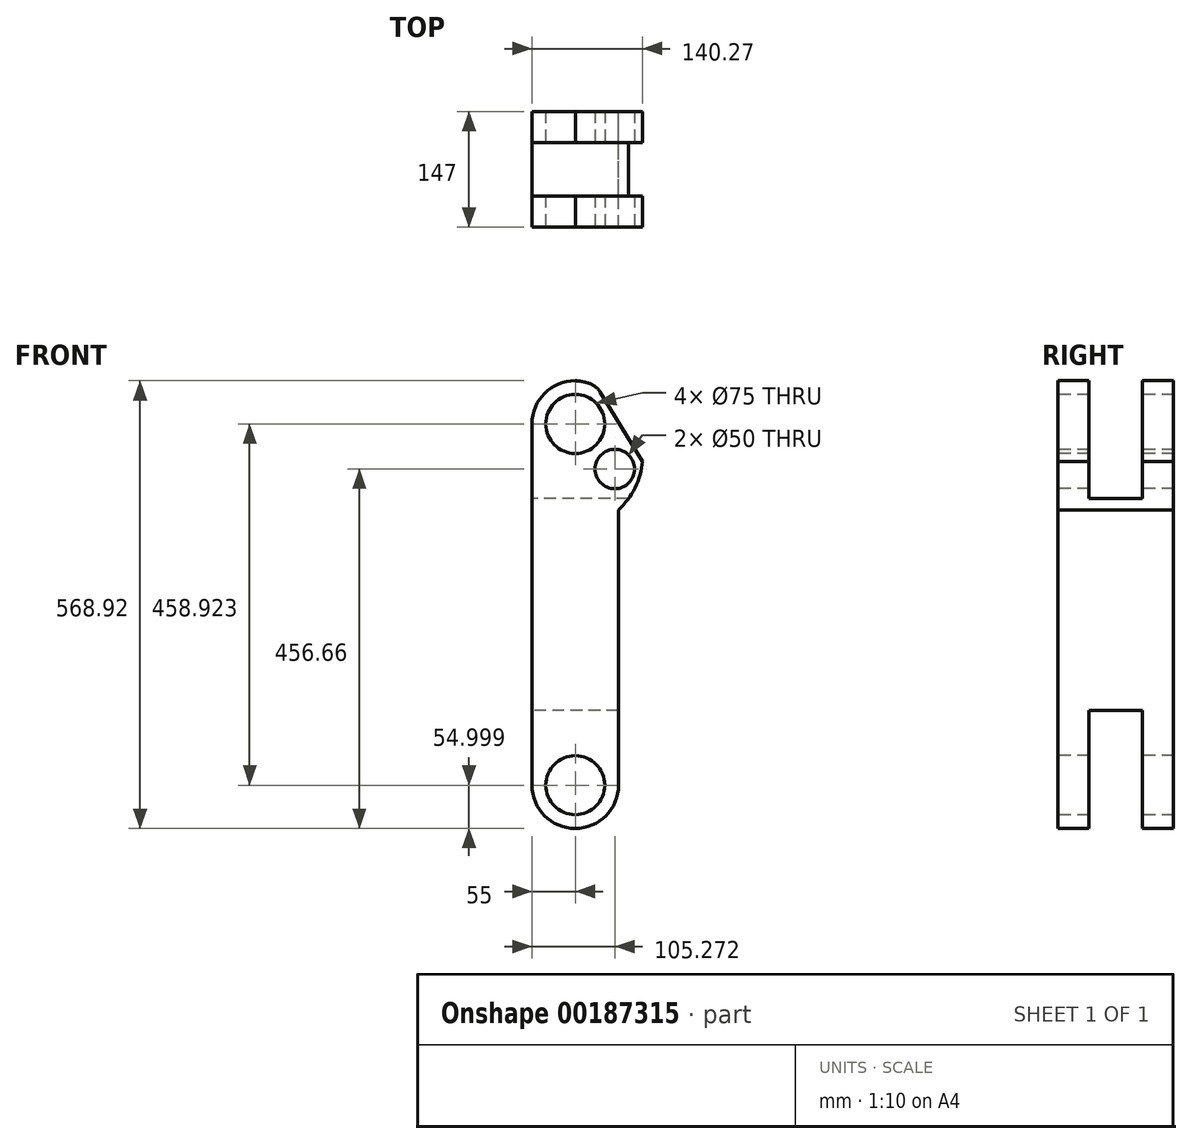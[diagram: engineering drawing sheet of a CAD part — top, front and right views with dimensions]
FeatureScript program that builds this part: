
annotation { "Feature Type Name" : "Feature", "Feature Type Description" : "" }
export const myFeature = defineFeature(function(context is Context, id is Id, definition is map)
    precondition{}
    {
        {
            var Q0;
            Q0=qCreatedBy(makeId("Front.planeOp"),FACE);
            var sketch = newSketch(context, id + "F0", { "sketchPlane" : qUnion([Q0])});
            skLineSegment(sketch, "E0.bottom", {"start": v(0, 284.46) * mm, "end": v(0, 284.46) * mm});
            skLineSegment(sketch, "E0.top", {"start": v(0, -284.46) * mm, "end": v(0, -284.46) * mm});
            skLineSegment(sketch, "E0.left", {"start": v(55, 120.38) * mm, "end": v(55, -229.46) * mm});
            skLineSegment(sketch, "E0.right", {"start": v(-55, 229.46) * mm, "end": v(-55, -229.46) * mm});
            skPoint(sketch, "E0.middle", {"position": v(0, 0) * mm});
            skPoint(sketch, "E1.visualSharp", {"position": v(-55, 284.46) * mm});
            skArc(sketch, "E1.filletArc", {"start": v(0, 284.46) * mm, "mid": v(-38.9, 268.35) * mm, "end": v(-55, 229.46) * mm});
            skPoint(sketch, "E2.visualSharp", {"position": v(55, 284.46) * mm});
            skPoint(sketch, "E3.visualSharp", {"position": v(-55, -284.46) * mm});
            skArc(sketch, "E3.filletArc", {"start": v(-55, -229.46) * mm, "mid": v(-38.9, -268.35) * mm, "end": v(0, -284.46) * mm});
            skPoint(sketch, "E4.visualSharp", {"position": v(55, -284.46) * mm});
            skArc(sketch, "E4.filletArc", {"start": v(0, -284.46) * mm, "mid": v(38.9, -268.35) * mm, "end": v(55, -229.46) * mm});
            skArc(sketch, "E5", {"start": v(55, 120.38) * mm, "mid": v(80.7, 220.25) * mm, "end": v(0, 284.46) * mm});
            skSolve(sketch);
        }
        {
            var Q0;
            Q0=qSketchRegion(id+"F0",true);
            extrude(context, id + "F1", {"entities" : qUnion([Q0]), "depth" : 147 * mm});
        }
        {
            var Q0;
            Q0=makeQuery(id+"F1.opExtrude","CAP_FACE",FACE,{"disambiguationData":[OSD([sQuery(id+"F0.wireOp",EDGE,"E0.left"),sQuery(id+"F0.wireOp",EDGE,"E0.right"),sQuery(id+"F0.wireOp",EDGE,"E1.filletArc"),sQuery(id+"F0.wireOp",EDGE,"E3.filletArc"),sQuery(id+"F0.wireOp",EDGE,"E4.filletArc"),sQuery(id+"F0.wireOp",EDGE,"AnRb1Ur5-qgVB-Ir7P-44gH-ltZYmHFHPQIi"),sQuery(id+"F0.wireOp",EDGE,"Xsvl4XlF-l4KZ-kMPT-x2mh-j82rKu8JnjOS"),sQuery(id+"F0.wireOp",EDGE,"CMO7md0D-hhAI-clTv-zCRc-Xt4Ap3c6JHup")])],"isStart":false});
            var sketch = newSketch(context, id + "F2", { "sketchPlane" : qUnion([Q0])});
            skCircle(sketch, "E6", {"center": v(0, 229.46) * mm, "radius": 37.5 * mm});
            skCircle(sketch, "E7", {"center": v(0, -229.46) * mm, "radius": 37.5 * mm});
            skCircle(sketch, "E8", {"center": v(50.27, 172.2) * mm, "radius": 25 * mm});
            skSolve(sketch);
        }
        {
            var Q0;
            Q0 = qSketchRegion(id + "F2", true);
            extrude(context, id + "F3", {"entities" : qUnion([Q0]), "operationType" : NewBodyOperationType.REMOVE, "endBound" : BoundingType.THROUGH_ALL, "oppositeDirection" : true, "depth" : 25 * mm});
        }
        {
            var Q0;
            Q0=makeQuery(id+"F1.opExtrude","CAP_FACE",FACE,{"disambiguationData":[OSD([sQuery(id+"F0.wireOp",EDGE,"E0.left"),sQuery(id+"F0.wireOp",EDGE,"E0.right"),sQuery(id+"F0.wireOp",EDGE,"E1.filletArc"),sQuery(id+"F0.wireOp",EDGE,"E3.filletArc"),sQuery(id+"F0.wireOp",EDGE,"E4.filletArc"),sQuery(id+"F0.wireOp",EDGE,"E5")])],"isStart":false});
            var sketch = newSketch(context, id + "F4", { "sketchPlane" : qUnion([Q0])});
            skLineSegment(sketch, "E9", {"start": v(26.66, 277.88) * mm, "end": v(85.27, 181.98) * mm});
            skSolve(sketch);
        }
        {
            var Q0;
            Q0 = qSketchRegion(id + "F4", true);
            var Q1;
            {var subQ0=sQuery(id+"F4.wireOp",EDGE,"E9");Q1=makeQuery(id+"F4.imprint","IMPRINT",FACE,{"disambiguationData":[TD([[makeQuery(id+"F4.imprint","IMPRINT",EDGE,{"derivedFrom":subQ0}),1.0]])]});}
            extrude(context, id + "F5", {"entities" : qUnion([Q0, Q1]), "operationType" : NewBodyOperationType.REMOVE, "endBound" : BoundingType.THROUGH_ALL, "oppositeDirection" : true, "depth" : 25 * mm});
        }
        {
            var Q0;
            {var subQ0=sQuery(id+"F4.wireOp",EDGE,"E9");var subQ1=sQuery(id+"F0.wireOp",EDGE,"E5");Q0=makeQuery(id+"F5.boolean.opBoolean","COPY",EDGE,{"derivedFrom":makeQuery(id+"F5.opExtrude","SWEPT_EDGE",EDGE,{"disambiguationData":[OSD([subQ1,subQ0]),TDD([makeQuery(id+"F4.imprint","INTERSECT",VERTEX,{"disambiguationData":[OD(0.0)],"derivedFrom":[makeQuery(id+"F1.opExtrude","CAP_EDGE",EDGE,{"disambiguationData":[OSD([subQ1])],"isStart":false}),subQ0]})])]})});}
            var Q1;
            {var subQ0=sQuery(id+"F4.wireOp",EDGE,"E9");var subQ1=sQuery(id+"F0.wireOp",EDGE,"E5");Q1=makeQuery(id+"F5.boolean.opBoolean","COPY",EDGE,{"derivedFrom":makeQuery(id+"F5.opExtrude","SWEPT_EDGE",EDGE,{"disambiguationData":[OSD([subQ1,subQ0]),TDD([makeQuery(id+"F4.imprint","INTERSECT",VERTEX,{"disambiguationData":[OD(1.0)],"derivedFrom":[makeQuery(id+"F1.opExtrude","CAP_EDGE",EDGE,{"disambiguationData":[OSD([subQ1])],"isStart":false}),subQ0]})])]})});}
            fillet(context, id + "F6", {"entities" : qUnion([Q0, Q1]), "radius" : 25 * mm, "tangentPropagation" : true, "allowEdgeOverflow" : false});
        }
        {
            var Q0;
            Q0=makeQuery(id+"F1.opExtrude","SWEPT_FACE",FACE,{"disambiguationData":[OSD([sQuery(id+"F0.wireOp",EDGE,"E0.right")])]});
            var sketch = newSketch(context, id + "F7", { "sketchPlane" : qUnion([Q0])});
            skLineSegment(sketch, "E10", {"start": v(107.3, -134.46) * mm, "end": v(107.3, -284.46) * mm});
            skLineSegment(sketch, "E11", {"start": v(107.3, -284.46) * mm, "end": v(39.7, -284.46) * mm});
            skLineSegment(sketch, "E12", {"start": v(39.7, -284.46) * mm, "end": v(39.7, -134.46) * mm});
            skLineSegment(sketch, "E13", {"start": v(39.7, -134.46) * mm, "end": v(107.3, -134.46) * mm});
            skLineSegment(sketch, "E14", {"start": v(39.7, -134.46) * mm, "end": v(0, -134.46) * mm, "construction": true});
            skLineSegment(sketch, "E15", {"start": v(107.3, -134.46) * mm, "end": v(147, -134.46) * mm, "construction": true});
            skLineSegment(sketch, "E16", {"start": v(147, 0) * mm, "end": v(0, 0) * mm, "construction": true});
            skLineSegment(sketch, "E17.MirrorCS", {"start": v(107.3, 284.46) * mm, "end": v(39.7, 284.46) * mm});
            skLineSegment(sketch, "E18.MirrorCS", {"start": v(39.7, 284.46) * mm, "end": v(39.7, 134.46) * mm});
            skLineSegment(sketch, "E19.MirrorCS", {"start": v(39.7, 134.46) * mm, "end": v(107.3, 134.46) * mm});
            skLineSegment(sketch, "E20.MirrorCS", {"start": v(107.3, 134.46) * mm, "end": v(107.3, 284.46) * mm});
            skSolve(sketch);
        }
        {
            var Q0;
            {var subQ0=sQuery(id+"F7.wireOp",EDGE,"E13");Q0=makeQuery(id+"F7.imprint","IMPRINT",FACE,{"disambiguationData":[TD([[makeQuery(id+"F7.imprint","IMPRINT",EDGE,{"derivedFrom":subQ0}),-1.0]])]});}
            var Q1;
            {var subQ0=sQuery(id+"F7.wireOp",EDGE,"E11");Q1=makeQuery(id+"F7.imprint","IMPRINT",FACE,{"disambiguationData":[TD([[makeQuery(id+"F7.imprint","IMPRINT",EDGE,{"derivedFrom":subQ0}),-1.0]])]});}
            var Q2;
            {var subQ0=sQuery(id+"F7.wireOp",EDGE,"E19.MirrorCS");Q2=makeQuery(id+"F7.imprint","IMPRINT",FACE,{"disambiguationData":[TD([[makeQuery(id+"F7.imprint","IMPRINT",EDGE,{"derivedFrom":subQ0}),1.0]])]});}
            var Q3;
            {var subQ0=sQuery(id+"F7.wireOp",EDGE,"E17.MirrorCS");Q3=makeQuery(id+"F7.imprint","IMPRINT",FACE,{"disambiguationData":[TD([[makeQuery(id+"F7.imprint","IMPRINT",EDGE,{"derivedFrom":subQ0}),1.0]])]});}
            extrude(context, id + "F8", {"entities" : qUnion([Q0, Q1, Q2, Q3]), "operationType" : NewBodyOperationType.REMOVE, "endBound" : BoundingType.THROUGH_ALL, "oppositeDirection" : true, "depth" : 25 * mm});
        }
    });
